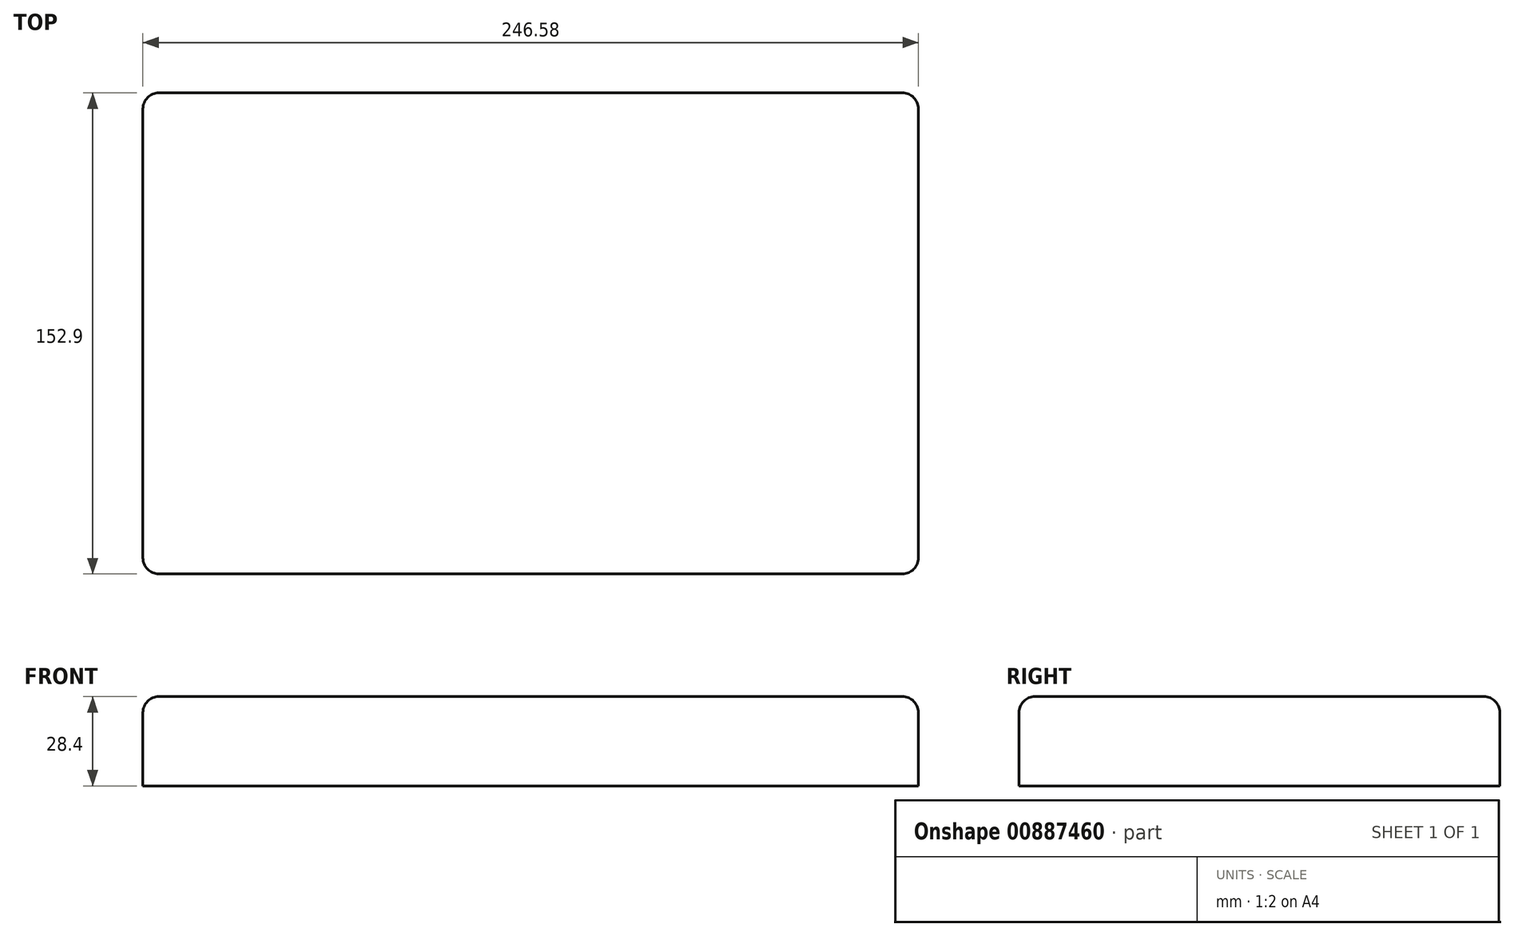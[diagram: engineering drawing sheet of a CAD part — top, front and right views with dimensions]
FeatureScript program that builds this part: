
annotation { "Feature Type Name" : "Feature", "Feature Type Description" : "" }
export const myFeature = defineFeature(function(context is Context, id is Id, definition is map)
    precondition{}
    {
        {
            var Q0;
            Q0=qCreatedBy(makeId("Top.planeOp"),FACE);
            var sketch = newSketch(context, id + "F0", { "sketchPlane" : qUnion([Q0])});
            skLineSegment(sketch, "E0.bottom", {"start": v(-123.3, 76.45) * mm, "end": v(123.3, 76.45) * mm});
            skLineSegment(sketch, "E0.top", {"start": v(-123.3, -76.45) * mm, "end": v(123.3, -76.45) * mm});
            skLineSegment(sketch, "E0.left", {"start": v(-123.3, 76.45) * mm, "end": v(-123.3, -76.45) * mm});
            skLineSegment(sketch, "E0.right", {"start": v(123.3, 76.45) * mm, "end": v(123.3, -76.45) * mm});
            skPoint(sketch, "E0.middle", {"position": v(0, 0) * mm});
            skSolve(sketch);
        }
        {
            var Q0;
            Q0=makeQuery(id+"F0.imprint","IMPRINT",FACE,{"disambiguationData":[TD([[makeQuery(id+"F0.imprint","IMPRINT",EDGE,{"derivedFrom":sQuery(id+"F0.wireOp",EDGE,"E0.bottom")}),-1.0]])]});
            extrude(context, id + "F1", {"entities" : qUnion([Q0]), "depth" : 3 * mm, "offsetDistance" : 25.4 * mm, "hasSecondDirection" : true, "secondDirectionOppositeDirection" : true, "secondDirectionDepth" : 25.4 * mm});
        }
        {
            var Q0;
            Q0=makeQuery(id+"F1.opExtrude","CAP_EDGE",EDGE,{"disambiguationData":[OSD([sQuery(id+"F0.wireOp",EDGE,"E0.right")])],"isStart":false});
            fillet(context, id + "F2", {"entities" : qUnion([Q0]), "radius" : 5.08 * mm, "tangentPropagation" : true, "allowEdgeOverflow" : false});
        }
        {
            var Q0;
            Q0=makeQuery(id+"F1.opExtrude","CAP_EDGE",EDGE,{"disambiguationData":[OSD([sQuery(id+"F0.wireOp",EDGE,"E0.top")])],"isStart":false});
            var Q1;
            Q1=makeQuery(id+"F1.opExtrude","CAP_EDGE",EDGE,{"disambiguationData":[OSD([sQuery(id+"F0.wireOp",EDGE,"E0.bottom")])],"isStart":false});
            var Q2;
            Q2=makeQuery(id+"F1.opExtrude","CAP_EDGE",EDGE,{"disambiguationData":[OSD([sQuery(id+"F0.wireOp",EDGE,"E0.left")])],"isStart":false});
            var Q3;
            Q3=makeQuery(id+"F1.opExtrude","SWEPT_EDGE",EDGE,{"disambiguationData":[OSD([sQuery(id+"F0.wireOp",EDGE,"E0.top"),sQuery(id+"F0.wireOp",EDGE,"E0.right")])]});
            var Q4;
            Q4=makeQuery(id+"F1.opExtrude","SWEPT_EDGE",EDGE,{"disambiguationData":[OSD([sQuery(id+"F0.wireOp",EDGE,"E0.bottom"),sQuery(id+"F0.wireOp",EDGE,"E0.right")])]});
            var Q5;
            Q5=makeQuery(id+"F1.opExtrude","SWEPT_EDGE",EDGE,{"disambiguationData":[OSD([sQuery(id+"F0.wireOp",EDGE,"E0.top"),sQuery(id+"F0.wireOp",EDGE,"E0.left")])]});
            var Q6;
            Q6=makeQuery(id+"F1.opExtrude","SWEPT_EDGE",EDGE,{"disambiguationData":[OSD([sQuery(id+"F0.wireOp",EDGE,"E0.bottom"),sQuery(id+"F0.wireOp",EDGE,"E0.left")])]});
            fillet(context, id + "F3", {"entities" : qUnion([Q0, Q1, Q2, Q3, Q4, Q5, Q6]), "radius" : 5.08 * mm, "tangentPropagation" : true, "allowEdgeOverflow" : false});
        }
    });
